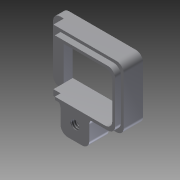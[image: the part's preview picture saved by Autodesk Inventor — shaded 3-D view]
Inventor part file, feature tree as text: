
AUTODESK INVENTOR PART (.ipt)
format: ipt  version: 2011 (Build 150239000, 239)  size: 181,760 bytes
history: native  units: in
note: dims shown in document units (in); Inventor stores cm internally (conversion verified against a paired STEP export)
features: sketch x7, extrude x6, fillet x1, hole x1
ambient origin geometry x8: Origin, YZ Plane, XZ Plane, XY Plane, X Axis, Y Axis, Z Axis, Center Point
bodies: Solid1 (feature_tree)
feature tree (15):
  extrude  "Extrusion1"  Depth=0.3543in
  extrude  "Extrusion2"  Depth=0.1378in
  extrude  "Extrusion3"  Depth=0.0315in
  extrude  "Extrusion4"  Depth=0.0315in
  fillet  "Fillet1"  Radius=0.1378in
  hole  "Hole2"  [1 undecoded]
  extrude  "Extrusion5"  Depth=0.0157in
  extrude  "Extrusion6"  Depth=0.1575in TaperAngle=0.0deg
  sketch  "Sketch1"  dims[d0=0.2756in d1=0.3543in]
  sketch  "Sketch2"  dims[d2=0.1772in d3=0.1378in]
  sketch  "Sketch3"  dims[d4=0.0591in d5=0.0315in]
  sketch  "Sketch4"  dims[d6=0.0315in d7=0.0315in d8=0.1378in d9=0.0in]
  sketch  "Sketch6"  dims[d10=0.0886in d11=0.0in d12=0.0157in]
  sketch  "Sketch7"  dims[d13=0.0157in d14=0.0157in]
  sketch  "Sketch8"  dims[d15=0.0315in d16=0.0in d19=0.1575in d20=0.0in d21=0.0394in d29=0.0394in d30=0.1575in d31=0.047in d32=0.75in d33=0.375in d34=0.25in d35=0.5635in d36=1.0in d37=0.8108in d38=0.0394in d39=0.0in d40=0.0394in d41=0.0in]
note: 1 required parameter value undecoded (feature->parameter linkage not recoverable at this tier; creation-order binding heuristic only, values carry confidence <= 0.55)
